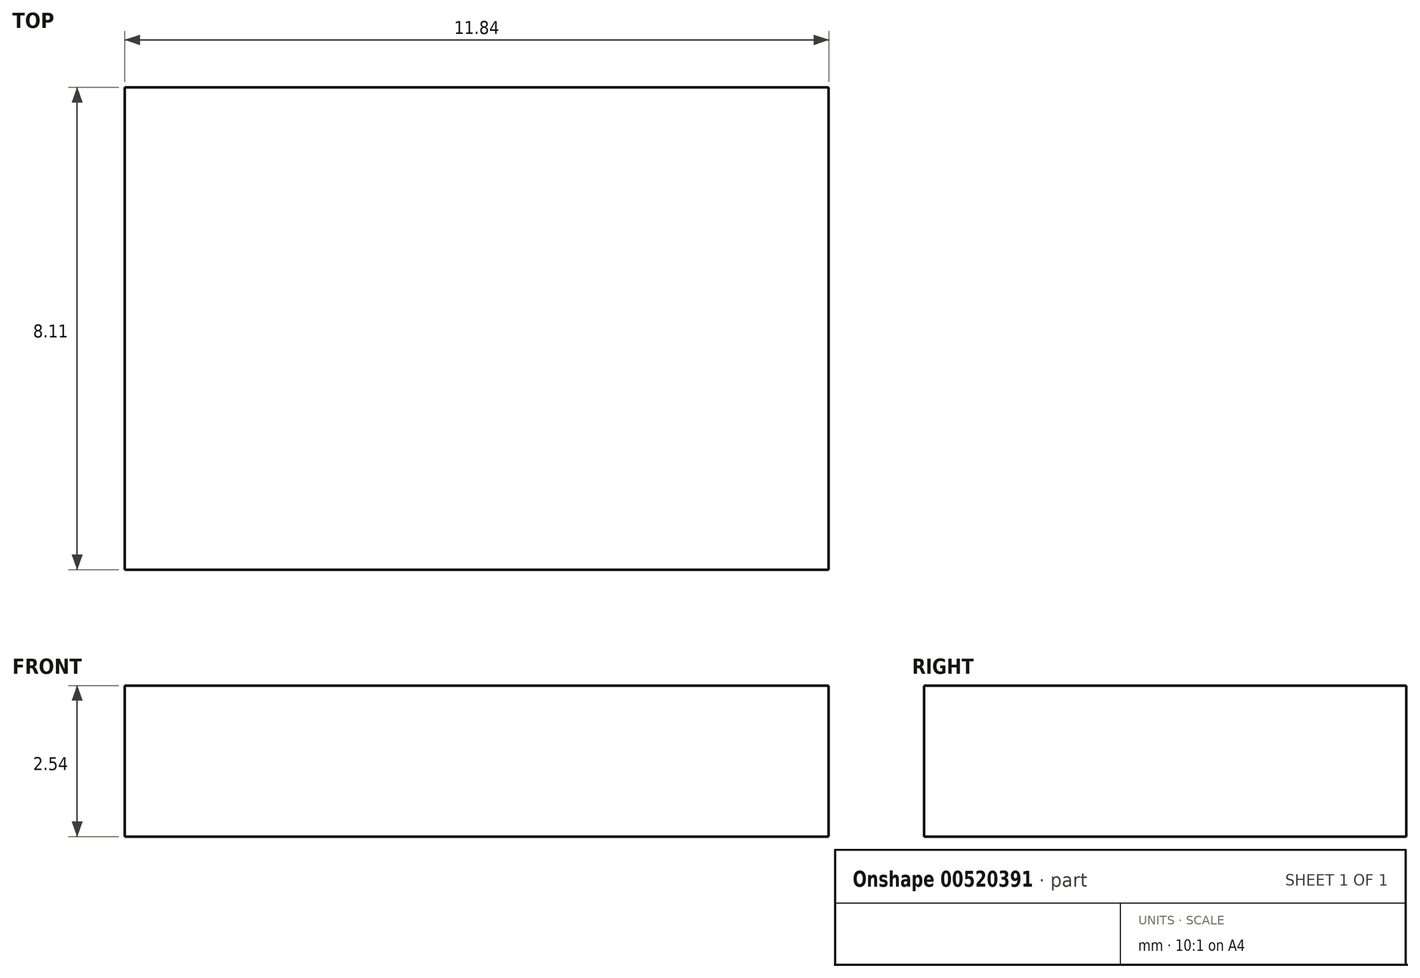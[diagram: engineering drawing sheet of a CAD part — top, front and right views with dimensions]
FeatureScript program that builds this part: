
annotation { "Feature Type Name" : "Feature", "Feature Type Description" : "" }
export const myFeature = defineFeature(function(context is Context, id is Id, definition is map)
    precondition{}
    {
        {
            var Q0;
            Q0=qCreatedBy(makeId("Top.planeOp"),FACE);
            var sketch = newSketch(context, id + "F0", { "sketchPlane" : qUnion([Q0])});
            skLineSegment(sketch, "E0", {"start": v(0, 0) * mm, "end": v(-5.92, 0) * mm});
            skPoint(sketch, "E1", {"position": v(0, 0) * mm});
            skLineSegment(sketch, "E2", {"start": v(0, 0) * mm, "end": v(0, 8.11) * mm});
            skLineSegment(sketch, "E3.MirrorCS", {"start": v(0, 0) * mm, "end": v(5.92, 0) * mm});
            skLineSegment(sketch, "E4", {"start": v(5.92, 0) * mm, "end": v(5.92, 8.11) * mm});
            skLineSegment(sketch, "E5", {"start": v(5.92, 8.11) * mm, "end": v(0, 8.11) * mm});
            skLineSegment(sketch, "E6", {"start": v(0, 8.11) * mm, "end": v(-5.92, 8.11) * mm});
            skLineSegment(sketch, "E7", {"start": v(-5.92, 8.11) * mm, "end": v(-5.92, 0) * mm});
            skSolve(sketch);
        }
        {
            var Q0;
            Q0 = qSketchRegion(id + "F0", true);
            extrude(context, id + "F1", {"entities" : qUnion([Q0]), "depth" : 2.54 * mm, "offsetDistance" : 25.4 * mm});
        }
    });
